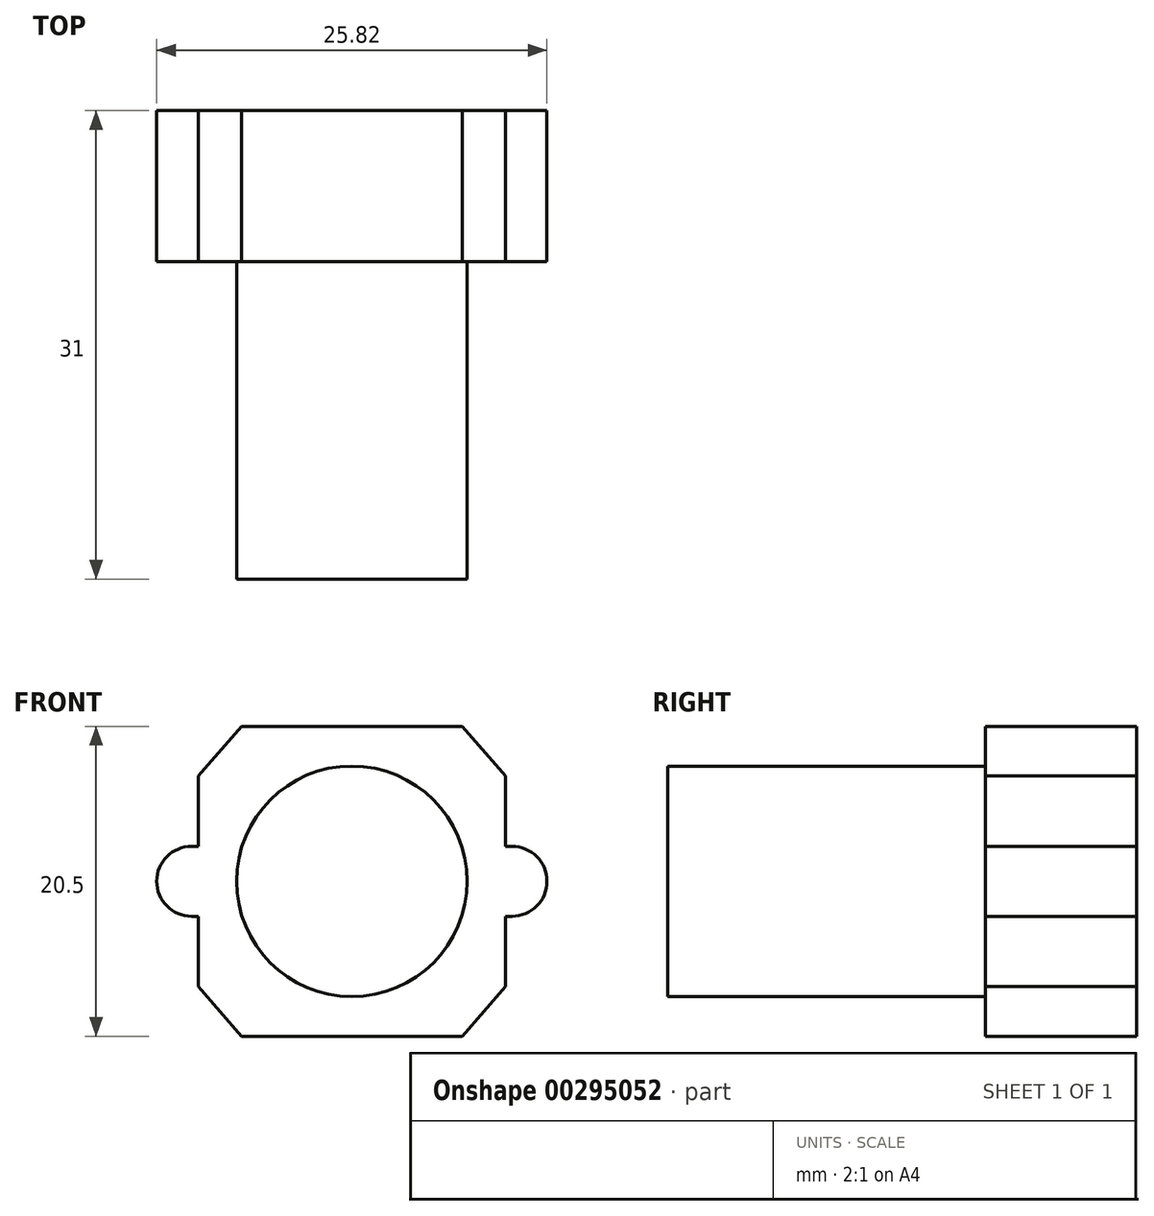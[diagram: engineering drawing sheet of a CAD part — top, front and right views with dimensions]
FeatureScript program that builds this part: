
annotation { "Feature Type Name" : "Feature", "Feature Type Description" : "" }
export const myFeature = defineFeature(function(context is Context, id is Id, definition is map)
    precondition{}
    {
        {
            var Q0;
            Q0=qCreatedBy(makeId("Front.planeOp"),FACE);
            var sketch = newSketch(context, id + "F0", { "sketchPlane" : qUnion([Q0])});
            skLineSegment(sketch, "E0", {"start": v(-10.15, 6.96) * mm, "end": v(-7.3, 10.25) * mm});
            skLineSegment(sketch, "E1", {"start": v(-7.3, 10.25) * mm, "end": v(7.3, 10.25) * mm});
            skLineSegment(sketch, "E2", {"start": v(7.3, 10.25) * mm, "end": v(10.15, 6.96) * mm});
            skLineSegment(sketch, "E3", {"start": v(10.15, 6.96) * mm, "end": v(10.15, -6.96) * mm});
            skLineSegment(sketch, "E4", {"start": v(10.15, -6.96) * mm, "end": v(7.3, -10.25) * mm});
            skLineSegment(sketch, "E5", {"start": v(7.3, -10.25) * mm, "end": v(-7.3, -10.25) * mm});
            skLineSegment(sketch, "E6", {"start": v(-7.3, -10.25) * mm, "end": v(-10.15, -6.96) * mm});
            skLineSegment(sketch, "E7", {"start": v(-10.15, -6.96) * mm, "end": v(-10.15, 6.96) * mm});
            skPoint(sketch, "E8", {"position": v(-10.15, 0) * mm});
            skPoint(sketch, "E9", {"position": v(0, 10.25) * mm});
            skLineSegment(sketch, "E10", {"start": v(10.15, 2.31) * mm, "end": v(10.6, 2.31) * mm});
            skLineSegment(sketch, "E11", {"start": v(10.15, -2.31) * mm, "end": v(10.6, -2.31) * mm});
            skLineSegment(sketch, "E12", {"start": v(10.6, 2.31) * mm, "end": v(10.6, 0) * mm, "construction": true});
            skLineSegment(sketch, "E13", {"start": v(10.6, -2.31) * mm, "end": v(10.6, 0) * mm, "construction": true});
            skLineSegment(sketch, "E14", {"start": v(-10.15, 2.32) * mm, "end": v(-10.6, 2.32) * mm});
            skLineSegment(sketch, "E15", {"start": v(-10.15, -2.32) * mm, "end": v(-10.6, -2.32) * mm});
            skLineSegment(sketch, "E16", {"start": v(-10.6, 2.31) * mm, "end": v(-10.6, 0) * mm, "construction": true});
            skLineSegment(sketch, "E17", {"start": v(-10.6, -2.32) * mm, "end": v(-10.6, 0) * mm, "construction": true});
            skArc(sketch, "E18", {"start": v(10.6, 2.31) * mm, "mid": v(12.91, 0) * mm, "end": v(10.6, -2.32) * mm});
            skArc(sketch, "E19", {"start": v(-10.6, 2.32) * mm, "mid": v(-12.91, 0) * mm, "end": v(-10.6, -2.32) * mm});
            skSolve(sketch);
        }
        {
            var Q0;
            Q0 = qSketchRegion(id + "F0", true);
            extrude(context, id + "F1", {"entities" : qUnion([Q0]), "depth" : 10 * mm});
        }
        {
            var Q0;
            Q0=makeQuery(id+"F1.opExtrude","CAP_FACE",FACE,{"disambiguationData":[OSD([sQuery(id+"F0.wireOp",EDGE,"E0"),sQuery(id+"F0.wireOp",EDGE,"E1"),sQuery(id+"F0.wireOp",EDGE,"E2"),sQuery(id+"F0.wireOp",EDGE,"E3"),sQuery(id+"F0.wireOp",EDGE,"E4"),sQuery(id+"F0.wireOp",EDGE,"E5"),sQuery(id+"F0.wireOp",EDGE,"E6"),sQuery(id+"F0.wireOp",EDGE,"E7")])],"isStart":false});
            var sketch = newSketch(context, id + "F2", { "sketchPlane" : qUnion([Q0])});
            skCircle(sketch, "E20", {"center": v(0, 0) * mm, "radius": 7.63 * mm});
            skSolve(sketch);
        }
        {
            var Q0;
            Q0 = qSketchRegion(id + "F2", true);
            extrude(context, id + "F3", {"entities" : qUnion([Q0]), "operationType" : NewBodyOperationType.ADD, "depth" : 21 * mm});
        }
    });
